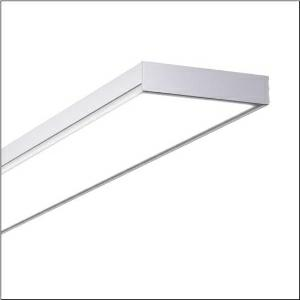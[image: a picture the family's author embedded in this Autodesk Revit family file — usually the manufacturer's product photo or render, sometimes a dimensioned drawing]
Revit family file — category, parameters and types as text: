
# Revit family: apollon_r__31_surface_51mp25wm2441ea_65a1
name_source: partatom
category: Lighting Fixtures
units: mm (PartAtom-declared; Revit-internal decimal feet)

## family parameters
Cut with Voids When Loaded = No
Host = Face
Light Source = No
Part Type = Normal
Room Calculation Point = No
Round Connector Dimension = Use Diameter
Shared = No

## types (1)
- Apollon® 31 Surface (1 x LED, 3800 lm, 27 W, 4000K)
    Apparent Load = 27 VA
    CIE Flux Codes = 61 87 97 97 100
    Color Rendering = 80
    Color Temperature = 4000K
    Default Elevation = 1800 mm
    Description = Apollon® 31 Surface, office luminaire, primary optical cover: micro prismatic cover, of PMMA, light emission: direct distribution, primary light characteristic: symmetric, installation type: surface-mounted, LED, rated luminous flux: 3.800lm, luminous efficacy: 139lm/W, light colour: 840, colour temperature: 4000K, control gear: ON/OFF Multilumen, with terminal, 3-pole, mains connection: 220..240V, AC, 50/60Hz, rated input power: 27W, housing, of sheet steel, coil coated, metallic grey (RAL 9006), length: 1.245mm, width: 200mm, height: 44mm, protection rating (complete): IP20, insulation class (complete): insulation class II (safety insulation), certification: CE, impact resistance: IK02, permissible operating ambient temperature: -20..+40°C, packaging unit: 1 piece
    Height = 44 mm
    Lamp = 1 x LED
    Lamp Light Flux = 3800 lm
    Lamp Power = 27 W
    Lamp count = 1
    Length = 1245 mm
    Luminous efficacy = 141 lm/W
    Manufacturer = Siteco
    ModVariant = No
    Model = 51MP25WM2441EA
    Mounting Place = Ceiling
    Mounting Type = Surface mounted
    Number of Poles = 1
    OnlyDefault = Yes
    Power Factor = 1
    Product Name = Apollon® 31 Surface
    Product group = office luminaire | ceiling mounted
    ProductGroupID = 302
    Protection Class = Protection class II
    Protection Degree = IP 20
    RLX_Detail_Level = 1
    RLX_Emergency_Light_Flux = 0 lm
    RLX_Emergency_Type = 0
    RLX_Emergency_Type_DB = No
    RlxData = <blob elided: 24097 chars, md5=ba346ebe>
    Socket = socket
    Standby Power = 0 W
    System Light Flux = 3800 lm
    System Power = 27 W
    Type Comments = Product without accessories
    Type Image = l_1313654.jpg
    URL = http://relux.com
    VarID = ---
    Voltage = 0 V
    Weight = 0.00 kg
    Width = 200 mm

## geometry (parser evidence)
native form markers: Blend x4, Sweep x11
no freeform markers — native parametric forms only
